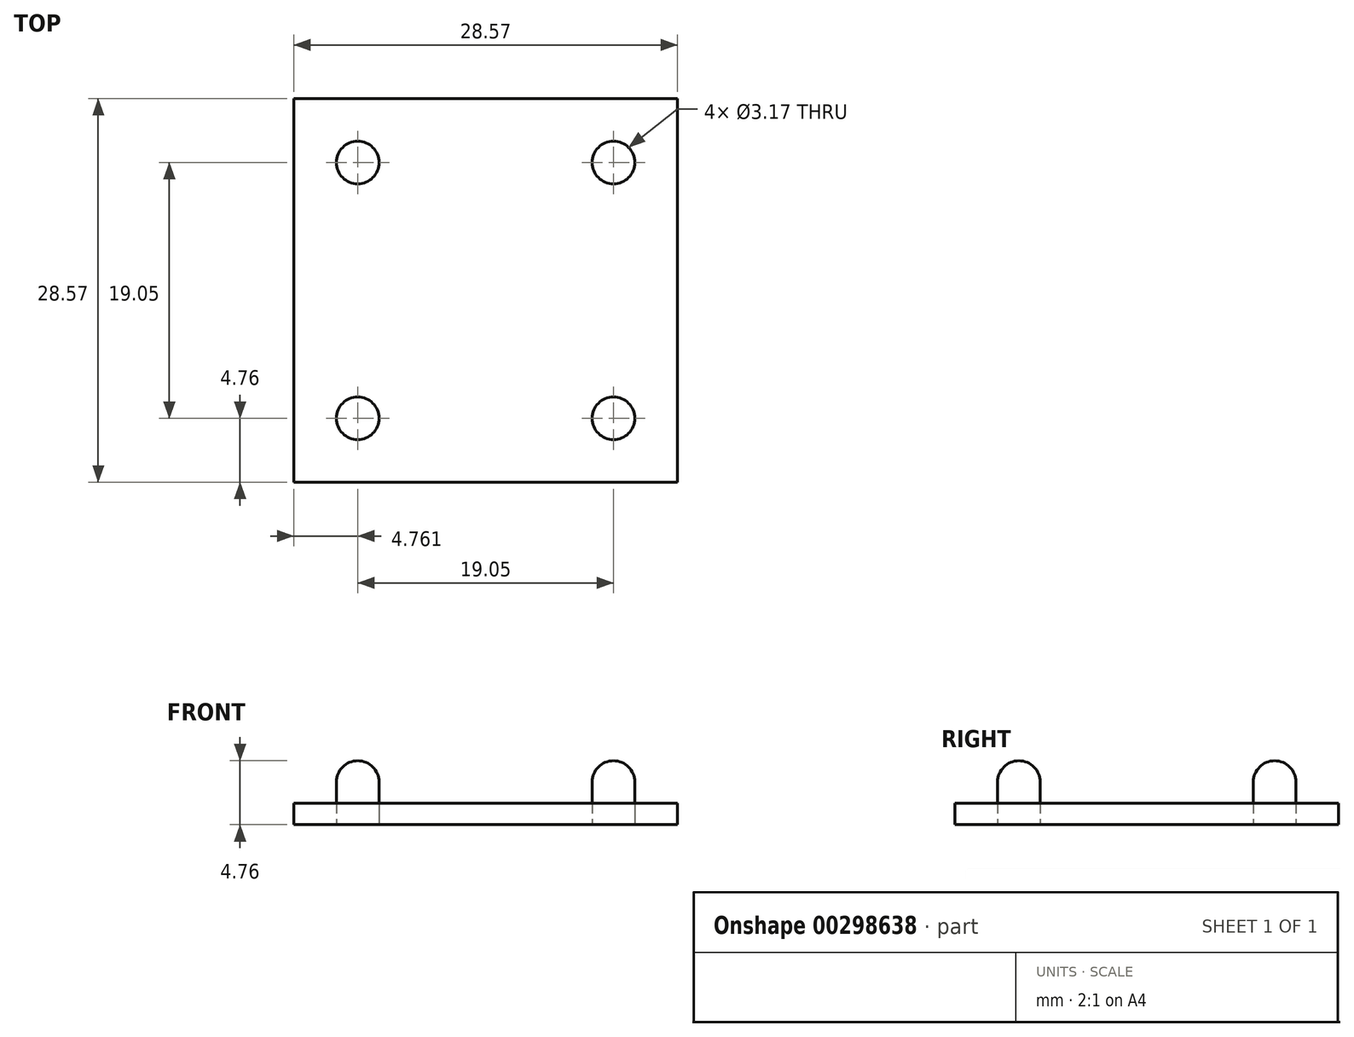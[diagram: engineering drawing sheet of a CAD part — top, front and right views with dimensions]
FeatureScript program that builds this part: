
annotation { "Feature Type Name" : "Feature", "Feature Type Description" : "" }
export const myFeature = defineFeature(function(context is Context, id is Id, definition is map)
    precondition{}
    {
        {
            var Q0;
            Q0=qCreatedBy(makeId("Top.planeOp"),FACE);
            var sketch = newSketch(context, id + "F0", { "sketchPlane" : qUnion([Q0])});
            skLineSegment(sketch, "E0.bottom", {"start": v(2.71, -4.76) * mm, "end": v(-25.86, -4.76) * mm});
            skLineSegment(sketch, "E0.top", {"start": v(2.71, 23.81) * mm, "end": v(-25.86, 23.81) * mm});
            skLineSegment(sketch, "E0.left", {"start": v(2.71, -4.76) * mm, "end": v(2.71, 23.81) * mm});
            skLineSegment(sketch, "E0.right", {"start": v(-25.86, -4.76) * mm, "end": v(-25.86, 23.81) * mm});
            skCircle(sketch, "E1", {"center": v(-21.1, 19.05) * mm, "radius": 1.59 * mm});
            skCircle(sketch, "E2", {"center": v(-2.05, 19.05) * mm, "radius": 1.59 * mm});
            skCircle(sketch, "E3", {"center": v(-21.1, 0) * mm, "radius": 1.59 * mm});
            skCircle(sketch, "E4", {"center": v(-2.05, 0) * mm, "radius": 1.59 * mm});
            skSolve(sketch);
        }
        {
            var Q0;
            Q0=makeQuery(id+"F0.imprint","IMPRINT",FACE,{"disambiguationData":[TD([[makeQuery(id+"F0.imprint","IMPRINT",EDGE,{"derivedFrom":sQuery(id+"F0.wireOp",EDGE,"E1")}),1.0]])]});
            var Q1;
            Q1=makeQuery(id+"F0.imprint","IMPRINT",FACE,{"disambiguationData":[TD([[makeQuery(id+"F0.imprint","IMPRINT",EDGE,{"derivedFrom":sQuery(id+"F0.wireOp",EDGE,"E2")}),1.0]])]});
            var Q2;
            Q2=makeQuery(id+"F0.imprint","IMPRINT",FACE,{"disambiguationData":[TD([[makeQuery(id+"F0.imprint","IMPRINT",EDGE,{"derivedFrom":sQuery(id+"F0.wireOp",EDGE,"E4")}),1.0]])]});
            var Q3;
            Q3=makeQuery(id+"F0.imprint","IMPRINT",FACE,{"disambiguationData":[TD([[makeQuery(id+"F0.imprint","IMPRINT",EDGE,{"derivedFrom":sQuery(id+"F0.wireOp",EDGE,"E3")}),1.0]])]});
            extrude(context, id + "F1", {"entities" : qUnion([Q0, Q1, Q2, Q3]), "depth" : 3.17 * mm});
        }
        {
            var Q0;
            Q0 = qSketchRegion(id + "F0", true);
            extrude(context, id + "F2", {"entities" : qUnion([Q0]), "depth" : 1.59 * mm});
        }
        {
            var Q0;
            Q0=makeQuery(id+"F1.opExtrude","CAP_FACE",FACE,{"disambiguationData":[OSD([sQuery(id+"F0.wireOp",EDGE,"E3")])],"isStart":false});
            var sketch = newSketch(context, id + "F3", { "sketchPlane" : qUnion([Q0])});
            skLineSegment(sketch, "E5", {"start": v(-19.51, 0) * mm, "end": v(-22.69, 0) * mm});
            skSolve(sketch);
        }
        {
            var Q0;
            {var subQ0=sQuery(id+"F3.wireOp",EDGE,"E5");Q0=makeQuery(id+"F3.imprint","IMPRINT",FACE,{"disambiguationData":[TD([[makeQuery(id+"F3.imprint","IMPRINT",EDGE,{"derivedFrom":subQ0}),-1.0]])]});}
            var Q1;
            Q1=sQuery(id+"F3.wireOp",EDGE,"E5");
            revolve(context, id + "F4", {"operationType" : NewBodyOperationType.ADD, "entities" : qUnion([Q0]), "axis" : qUnion([Q1]), "revolveType" : RevolveType.FULL});
        }
        {
            var Q0;
            Q0=makeQuery(id+"F1.opExtrude","CAP_FACE",FACE,{"disambiguationData":[OSD([sQuery(id+"F0.wireOp",EDGE,"E4")])],"isStart":false});
            var sketch = newSketch(context, id + "F5", { "sketchPlane" : qUnion([Q0])});
            skLineSegment(sketch, "E6", {"start": v(-0.46, 0) * mm, "end": v(-3.64, 0) * mm});
            skSolve(sketch);
        }
        {
            var Q0;
            {var subQ0=sQuery(id+"F5.wireOp",EDGE,"E6");Q0=makeQuery(id+"F5.imprint","IMPRINT",FACE,{"disambiguationData":[TD([[makeQuery(id+"F5.imprint","IMPRINT",EDGE,{"derivedFrom":subQ0}),-1.0]])]});}
            var Q1;
            Q1=sQuery(id+"F5.wireOp",EDGE,"E6");
            revolve(context, id + "F6", {"operationType" : NewBodyOperationType.ADD, "entities" : qUnion([Q0]), "axis" : qUnion([Q1]), "revolveType" : RevolveType.FULL});
        }
        {
            var Q0;
            Q0=makeQuery(id+"F1.opExtrude","CAP_FACE",FACE,{"disambiguationData":[OSD([sQuery(id+"F0.wireOp",EDGE,"E1")])],"isStart":false});
            var sketch = newSketch(context, id + "F7", { "sketchPlane" : qUnion([Q0])});
            skLineSegment(sketch, "E7", {"start": v(-21.1, 19.05) * mm, "end": v(-22.69, 19.05) * mm});
            skLineSegment(sketch, "E8", {"start": v(-22.69, 19.05) * mm, "end": v(-19.51, 19.05) * mm});
            skSolve(sketch);
        }
        {
            var Q0;
            {var subQ0=sQuery(id+"F7.wireOp",EDGE,"E8");var subQ3=makeQuery(id+"F7.imprint","IMPRINT",VERTEX,{"derivedFrom":subQ0});Q0=makeQuery(id+"F7.imprint","IMPRINT",FACE,{"disambiguationData":[TD([[makeQuery(id+"F7.imprint","IMPRINT",EDGE,{"disambiguationData":[TD([[subQ3,1.0]])],"derivedFrom":subQ0}),1.0]])]});}
            var Q1;
            Q1=sQuery(id+"F7.wireOp",EDGE,"E8");
            revolve(context, id + "F8", {"operationType" : NewBodyOperationType.ADD, "entities" : qUnion([Q0]), "axis" : qUnion([Q1]), "revolveType" : RevolveType.FULL});
        }
        {
            var Q0;
            Q0=makeQuery(id+"F1.opExtrude","CAP_FACE",FACE,{"disambiguationData":[OSD([sQuery(id+"F0.wireOp",EDGE,"E2")])],"isStart":false});
            var sketch = newSketch(context, id + "F9", { "sketchPlane" : qUnion([Q0])});
            skLineSegment(sketch, "E9", {"start": v(-2.05, 19.05) * mm, "end": v(-0.46, 19.05) * mm});
            skLineSegment(sketch, "E10", {"start": v(-0.46, 19.05) * mm, "end": v(-3.64, 19.05) * mm});
            skSolve(sketch);
        }
        {
            var Q0;
            {var subQ0=sQuery(id+"F9.wireOp",EDGE,"E10");var subQ3=makeQuery(id+"F9.imprint","IMPRINT",VERTEX,{"derivedFrom":subQ0});Q0=makeQuery(id+"F9.imprint","IMPRINT",FACE,{"disambiguationData":[TD([[makeQuery(id+"F9.imprint","IMPRINT",EDGE,{"disambiguationData":[TD([[subQ3,1.0]])],"derivedFrom":subQ0}),-1.0]])]});}
            var Q1;
            Q1=sQuery(id+"F9.wireOp",EDGE,"E10");
            revolve(context, id + "F10", {"operationType" : NewBodyOperationType.ADD, "entities" : qUnion([Q0]), "axis" : qUnion([Q1]), "revolveType" : RevolveType.FULL});
        }
    });
